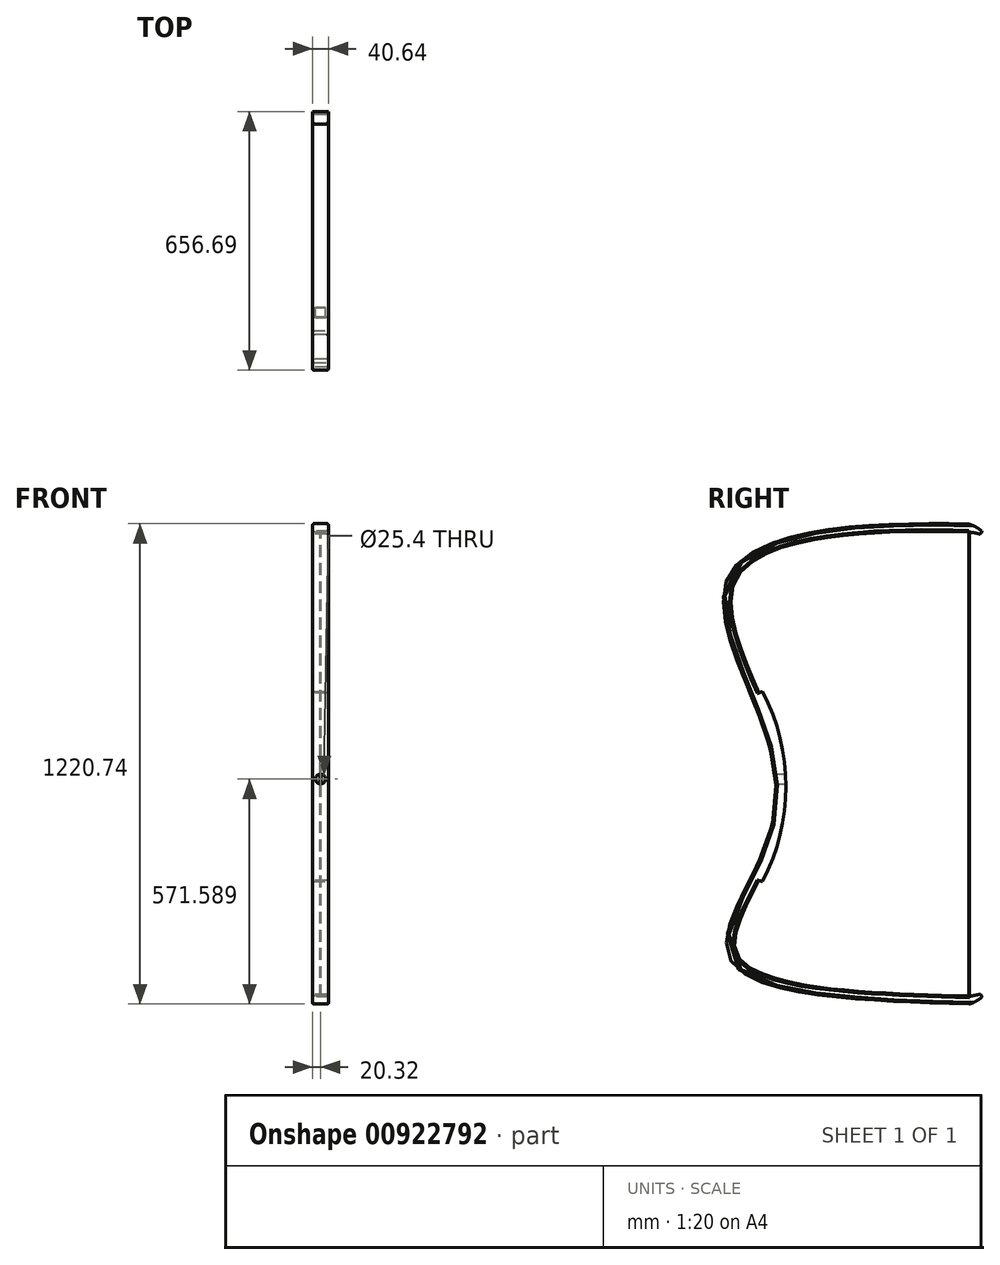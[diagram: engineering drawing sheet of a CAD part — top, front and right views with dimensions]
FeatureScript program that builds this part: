
annotation { "Feature Type Name" : "Feature", "Feature Type Description" : "" }
export const myFeature = defineFeature(function(context is Context, id is Id, definition is map)
    precondition{}
    {
        {
            var Q0;
            Q0=qCreatedBy(makeId("Right.planeOp"),FACE);
            var sketch = newSketch(context, id + "F0", { "sketchPlane" : qUnion([Q0])});
            skFitSpline(sketch, "E0", {"points": [v(0, 91.73) * mm, v(-76.53, 74.8) * mm, v(-65.03, 26.62) * mm, v(-65.02, -11.48) * mm, v(-76.25, -45.85) * mm, v(0, -60.67) * mm], "startDerivative": vector(-434, 12.9) * mm, "endDerivative": vector(444.14, -12.98) * mm});
            skFitSpline(sketch, "E1.0", {"points": [v(-0.08, 89.2) * mm, v(-4.57, 89.33) * mm, v(-13.56, 89.47) * mm, v(-26.63, 89.18) * mm, v(-38.94, 88.28) * mm, v(-50.09, 86.68) * mm, v(-59.69, 84.27) * mm, v(-66.04, 81.55) * mm, v(-69.93, 78.98) * mm, v(-72.22, 76.87) * mm, v(-73.61, 74.99) * mm, v(-74.42, 73.39) * mm, v(-75.04, 71.68) * mm, v(-75.5, 69.33) * mm, v(-75.58, 66.15) * mm, v(-75.2, 62.66) * mm, v(-74.15, 57.67) * mm, v(-71.97, 50.93) * mm, v(-68.57, 42.45) * mm, v(-65.6, 35.34) * mm, v(-63.44, 29.77) * mm, v(-62, 25.69) * mm, v(-60.83, 21.73) * mm, v(-59.6, 16.59) * mm, v(-58.69, 10.37) * mm, v(-58.69, 3.08) * mm, v(-59.63, -2.92) * mm, v(-60.94, -7.75) * mm, v(-62.21, -11.4) * mm, v(-63.77, -15.1) * mm, v(-65.51, -18.77) * mm, v(-67.35, -22.42) * mm, v(-69.17, -26) * mm, v(-70.87, -29.49) * mm, v(-72.37, -32.83) * mm, v(-73.55, -35.98) * mm, v(-74.32, -38.87) * mm, v(-74.62, -41.43) * mm, v(-74.46, -43.21) * mm, v(-74.1, -44.45) * mm, v(-73.7, -45.3) * mm, v(-73.15, -46.15) * mm, v(-72.2, -47.26) * mm, v(-70.54, -48.63) * mm, v(-67.83, -50.16) * mm, v(-64.45, -51.55) * mm, v(-59.12, -53.19) * mm, v(-51.1, -54.82) * mm, v(-39.78, -56.2) * mm, v(-27.2, -57.1) * mm, v(-13.79, -57.7) * mm, v(-4.55, -58) * mm, v(0.07, -58.13) * mm]});
            skArc(sketch, "E2", {"start": v(0.07, -58.13) * mm, "mid": v(1.6, -57.94) * mm, "end": v(3.1, -57.57) * mm});
            skArc(sketch, "E3", {"start": v(4, -58.43) * mm, "mid": v(3.77, -57.78) * mm, "end": v(3.1, -57.57) * mm});
            skArc(sketch, "E4", {"start": v(0, -60.67) * mm, "mid": v(2.14, -59.79) * mm, "end": v(4, -58.43) * mm});
            skArc(sketch, "E5.MirrorCS", {"start": v(0, 91.73) * mm, "mid": v(2.14, 90.86) * mm, "end": v(4, 89.5) * mm});
            skArc(sketch, "E6.MirrorCS", {"start": v(4, 89.5) * mm, "mid": v(3.76, 88.85) * mm, "end": v(3.09, 88.65) * mm});
            skArc(sketch, "E7.MirrorCS", {"start": v(-0.08, 89.2) * mm, "mid": v(1.52, 89.03) * mm, "end": v(3.09, 88.65) * mm});
            skSolve(sketch);
        }
        {
            var Q0;
            Q0=makeQuery(id+"F0.imprint","IMPRINT",FACE,{"disambiguationData":[TD([[makeQuery(id+"F0.imprint","IMPRINT",EDGE,{"derivedFrom":sQuery(id+"F0.wireOp",EDGE,"E0")}),1.0]])]});
            extrude(context, id + "F1", {"entities" : qUnion([Q0]), "endBound" : BoundingType.SYMMETRIC, "depth" : 5.08 * mm, "offsetDistance" : 25.4 * mm});
        }
        {
            var Q0;
            Q0=qCreatedBy(makeId("Right.planeOp"),FACE);
            var sketch = newSketch(context, id + "F2", { "sketchPlane" : qUnion([Q0])});
            skLineSegment(sketch, "E8", {"start": v(0, 89.53) * mm, "end": v(0, -58.73) * mm});
            skLineSegment(sketch, "E9.0", {"start": v(-0.13, 89.53) * mm, "end": v(-0.13, -58.73) * mm});
            skLineSegment(sketch, "E10", {"start": v(0, -58.73) * mm, "end": v(-0.13, -58.73) * mm});
            skLineSegment(sketch, "E11", {"start": v(0, 89.53) * mm, "end": v(-0.13, 89.53) * mm});
            skSolve(sketch);
        }
        {
            var Q0;
            Q0=makeQuery(id+"F2.imprint","IMPRINT",FACE,{"disambiguationData":[TD([[makeQuery(id+"F2.imprint","IMPRINT",EDGE,{"derivedFrom":sQuery(id+"F2.wireOp",EDGE,"E8")}),-1.0]])]});
            var Q1;
            Q1=sQuery(id+"F2.wireOp",EDGE,"E8");
            revolve(context, id + "F3", {"operationType" : NewBodyOperationType.ADD, "surfaceOperationType" : NewSurfaceOperationType.NEW, "entities" : qUnion([Q0]), "axis" : qUnion([Q1]), "revolveType" : RevolveType.FULL});
        }
        {
            var Q0;
            Q0=makeQuery(id+"F1.opExtrude","CAP_EDGE",EDGE,{"disambiguationData":[OSD([sQuery(id+"F0.wireOp",EDGE,"E0")])],"isStart":false});
            var Q1;
            Q1=makeQuery(id+"F1.opExtrude","CAP_EDGE",EDGE,{"disambiguationData":[OSD([sQuery(id+"F0.wireOp",EDGE,"E0")])],"isStart":true});
            var Q2;
            Q2=makeQuery(id+"F1.opExtrude","CAP_EDGE",EDGE,{"disambiguationData":[OSD([sQuery(id+"F0.wireOp",EDGE,"E1.0")])],"isStart":false});
            var Q3;
            Q3=makeQuery(id+"F1.opExtrude","CAP_EDGE",EDGE,{"disambiguationData":[OSD([sQuery(id+"F0.wireOp",EDGE,"E1.0")])],"isStart":true});
            fillet(context, id + "F4", {"entities" : qUnion([Q0, Q1, Q2, Q3]), "radius" : 0.5 * mm, "tangentPropagation" : true, "allowEdgeOverflow" : false});
        }
        {
            var Q0;
            Q0=makeQuery(id+"F1.opExtrude","CAP_FACE",FACE,{"disambiguationData":[OSD([sQuery(id+"F0.wireOp",EDGE,"E0"),sQuery(id+"F0.wireOp",EDGE,"E1.0"),sQuery(id+"F0.wireOp",EDGE,"E2"),sQuery(id+"F0.wireOp",EDGE,"E3"),sQuery(id+"F0.wireOp",EDGE,"E4"),sQuery(id+"F0.wireOp",EDGE,"E5.MirrorCS"),sQuery(id+"F0.wireOp",EDGE,"E6.MirrorCS"),sQuery(id+"F0.wireOp",EDGE,"E7.MirrorCS")])],"isStart":false});
            var sketch = newSketch(context, id + "F5", { "sketchPlane" : qUnion([Q0])});
            skArc(sketch, "E12", {"start": v(-68.5, -20.19) * mm, "mid": v(-61.47, 8.4) * mm, "end": v(-68.5, 37) * mm});
            skArc(sketch, "E13.0", {"start": v(-65.58, -21.72) * mm, "mid": v(-58.17, 8.4) * mm, "end": v(-65.58, 38.53) * mm});
            skArc(sketch, "E14", {"start": v(-68.5, -20.19) * mm, "mid": v(-67.18, -21.23) * mm, "end": v(-65.58, -21.72) * mm});
            skArc(sketch, "E15", {"start": v(-65.58, 38.53) * mm, "mid": v(-67.14, 37.97) * mm, "end": v(-68.5, 37) * mm});
            skSolve(sketch);
        }
        {
            var Q0;
            {var subQ0=sQuery(id+"F5.wireOp",EDGE,"E13.0");Q0=makeQuery(id+"F5.imprint","IMPRINT",FACE,{"disambiguationData":[TD([[makeQuery(id+"F5.imprint","IMPRINT",EDGE,{"derivedFrom":subQ0}),1.0]])]});}
            var Q1;
            {var subQ1=sQuery(id+"F5.wireOp",EDGE,"E12");var subQ2=sQuery(id+"F0.wireOp",EDGE,"E1.0");var subQ3=sQuery(id+"F0.wireOp",EDGE,"E0");var subQ4=makeQuery(id+"F1.opExtrude","CAP_FACE",FACE,{"disambiguationData":[OSD([subQ3,subQ2,sQuery(id+"F0.wireOp",EDGE,"E2"),sQuery(id+"F0.wireOp",EDGE,"E3"),sQuery(id+"F0.wireOp",EDGE,"E4"),sQuery(id+"F0.wireOp",EDGE,"E5.MirrorCS"),sQuery(id+"F0.wireOp",EDGE,"E6.MirrorCS"),sQuery(id+"F0.wireOp",EDGE,"E7.MirrorCS")])],"isStart":false});var subQ5=makeQuery(id+"F4.opFillet","BLEND_EDGE",EDGE,{"blendedFrom":[makeQuery(id+"F1.opExtrude","CAP_EDGE",EDGE,{"disambiguationData":[OSD([subQ3])],"isStart":false}),subQ4],"blendedInto":[subQ4]});var subQ13=makeQuery(id+"F5.imprint","INTERSECT",VERTEX,{"disambiguationData":[OD(1.0)],"derivedFrom":[subQ5,subQ1]});Q1=makeQuery(id+"F5.imprint","IMPRINT",FACE,{"disambiguationData":[TD([[makeQuery(id+"F5.imprint","IMPRINT",EDGE,{"disambiguationData":[TD([[subQ13,1.0]])],"derivedFrom":subQ1}),-1.0]])]});}
            extrude(context, id + "F6", {"entities" : qUnion([Q0, Q1]), "operationType" : NewBodyOperationType.ADD, "oppositeDirection" : true, "depth" : 5.08 * mm, "offsetDistance" : 25.4 * mm});
        }
        {
            var Q0;
            Q0=makeQuery(id+"F6.opExtrude","CAP_EDGE",EDGE,{"disambiguationData":[OSD([sQuery(id+"F5.wireOp",EDGE,"E13.0")])],"isStart":false});
            var Q1;
            Q1=makeQuery(id+"F6.opExtrude","CAP_EDGE",EDGE,{"disambiguationData":[OSD([sQuery(id+"F5.wireOp",EDGE,"E13.0")])],"isStart":true});
            fillet(context, id + "F7", {"entities" : qUnion([Q0, Q1]), "radius" : 0.25 * mm, "tangentPropagation" : true, "allowEdgeOverflow" : false});
        }
        {
            var Q0;
            Q0=qCreatedBy(makeId("Front.planeOp"),FACE);
            cPlane(context, id + "F8", {"entities" : qUnion([Q0]), "cplaneType" : CPlaneType.OFFSET, "offset" : 59.69 * mm, "width" : 152.4 * mm, "height" : 152.4 * mm});
        }
        {
            var Q0;
            Q0=makeQuery(id+"F1.opExtrude","SWEPT_BODY",BODY,{"disambiguationData":[OSD([sQuery(id+"F0.wireOp",EDGE,"E0"),sQuery(id+"F0.wireOp",EDGE,"E1.0"),sQuery(id+"F0.wireOp",EDGE,"E2"),sQuery(id+"F0.wireOp",EDGE,"E3"),sQuery(id+"F0.wireOp",EDGE,"E4"),sQuery(id+"F0.wireOp",EDGE,"E5.MirrorCS"),sQuery(id+"F0.wireOp",EDGE,"E6.MirrorCS"),sQuery(id+"F0.wireOp",EDGE,"E7.MirrorCS")])]});
            var Q1;
            Q1=qCreatedBy(makeId("Origin.pointOp"),VERTEX);
            transform(context, id + "F9", {"entities" : qUnion([Q0]), "transformType" : TransformType.SCALE_UNIFORMLY, "scale" : 8, "scalePoint" : qUnion([Q1]), "makeCopy" : false});
        }
        {
            var Q0;
            Q0=qCreatedBy(id+"F8.planeOp",FACE);
            var sketch = newSketch(context, id + "F10", { "sketchPlane" : qUnion([Q0])});
            skCircle(sketch, "E16", {"center": v(25.83, 19.74) * mm, "radius": 12.7 * mm});
            skSolve(sketch);
        }
        {
            var Q0;
            Q0=makeQuery(id+"F10.imprint","IMPRINT",FACE,{"disambiguationData":[TD([[makeQuery(id+"F10.imprint","IMPRINT",EDGE,{"derivedFrom":sQuery(id+"F10.wireOp",EDGE,"E16")}),1.0]])]});
            extrude(context, id + "F11", {"entities" : qUnion([Q0]), "operationType" : NewBodyOperationType.REMOVE, "oppositeDirection" : true, "depth" : 25.4 * mm, "offsetDistance" : 25.4 * mm, "hasSecondDirection" : true, "secondDirectionOppositeDirection" : false, "secondDirectionDepth" : 25.4 * mm});
        }
        {
            var Q0;
            Q0=qCreatedBy(id+"F8.planeOp",FACE);
            cPlane(context, id + "F12", {"entities" : qUnion([Q0]), "cplaneType" : CPlaneType.OFFSET, "offset" : 406.4 * mm, "width" : 152.4 * mm, "height" : 152.4 * mm});
        }
        {
            var Q0;
            Q0=qCreatedBy(id+"F12.planeOp",FACE);
            var sketch = newSketch(context, id + "F13", { "sketchPlane" : qUnion([Q0])});
            skCircle(sketch, "E17", {"center": v(0, 86.26) * mm, "radius": 12.7 * mm});
            skSolve(sketch);
        }
        {
            var Q0;
            Q0=makeQuery(id+"F13.imprint","IMPRINT",FACE,{"disambiguationData":[TD([[makeQuery(id+"F13.imprint","IMPRINT",EDGE,{"derivedFrom":sQuery(id+"F13.wireOp",EDGE,"E17")}),1.0]])]});
            extrude(context, id + "F14", {"entities" : qUnion([Q0]), "operationType" : NewBodyOperationType.REMOVE, "depth" : 254 * mm, "offsetDistance" : 25.4 * mm, "hasSecondDirection" : true, "secondDirectionOppositeDirection" : true, "secondDirectionDepth" : 25.4 * mm});
        }
    });
